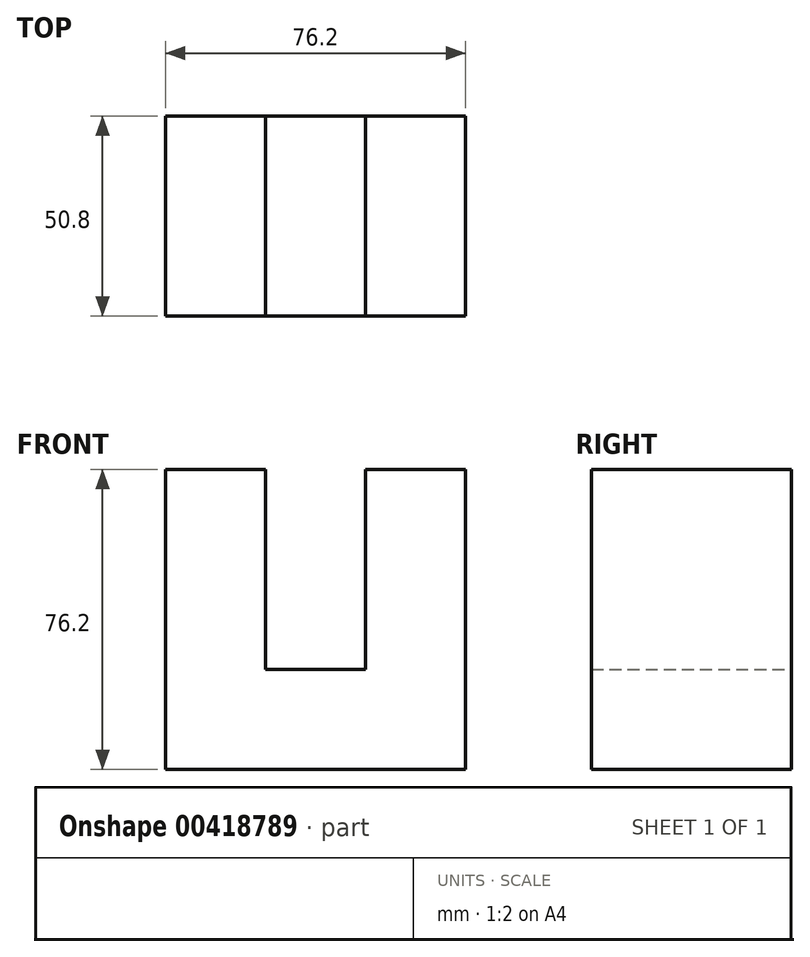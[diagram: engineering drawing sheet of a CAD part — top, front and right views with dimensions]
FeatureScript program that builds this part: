
annotation { "Feature Type Name" : "Feature", "Feature Type Description" : "" }
export const myFeature = defineFeature(function(context is Context, id is Id, definition is map)
    precondition{}
    {
        {
            var Q0;
            Q0=qCreatedBy(makeId("Front.planeOp"),FACE);
            var sketch = newSketch(context, id + "F0", { "sketchPlane" : qUnion([Q0])});
            skLineSegment(sketch, "E0", {"start": v(0, 0) * mm, "end": v(0, -76.2) * mm});
            skLineSegment(sketch, "E1", {"start": v(0, -76.2) * mm, "end": v(76.2, -76.2) * mm});
            skLineSegment(sketch, "E2", {"start": v(76.2, -76.2) * mm, "end": v(76.2, 0) * mm});
            skLineSegment(sketch, "E3", {"start": v(76.2, 0) * mm, "end": v(50.8, 0) * mm});
            skLineSegment(sketch, "E4", {"start": v(50.8, 0) * mm, "end": v(50.8, -50.8) * mm});
            skLineSegment(sketch, "E5", {"start": v(50.8, -50.8) * mm, "end": v(25.4, -50.8) * mm});
            skLineSegment(sketch, "E6", {"start": v(25.4, -50.8) * mm, "end": v(25.4, 0) * mm});
            skLineSegment(sketch, "E7", {"start": v(25.4, 0) * mm, "end": v(0, 0) * mm});
            skSolve(sketch);
        }
        {
            var Q0;
            Q0=makeQuery(id+"F0.imprint","IMPRINT",FACE,{"disambiguationData":[TD([[makeQuery(id+"F0.imprint","IMPRINT",EDGE,{"derivedFrom":sQuery(id+"F0.wireOp",EDGE,"E0")}),1.0]])]});
            extrude(context, id + "F1", {"entities" : qUnion([Q0]), "depth" : 50.8 * mm});
        }
    });
